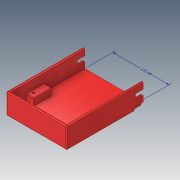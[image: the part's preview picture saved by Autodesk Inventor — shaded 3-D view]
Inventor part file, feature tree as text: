
AUTODESK INVENTOR PART (.ipt)
format: ipt  version: 2019 (Build 230136000, 136)  size: 272,384 bytes
history: native  units: mm
features: extrude x9, sketch x8, plane x3, projected_geometry x3, other x2, fillet x2
ambient origin geometry x8: Origin, YZ Plane, XZ Plane, XY Plane, X Axis, Y Axis, Z Axis, Center Point
bodies: Solid1 (feature_tree)
feature tree (27):
  other  "Annotations"
  extrude  "Extrusion1"  Depth=150.0mm
  extrude  "Extrusion2"  Depth=5.0mm
  extrude  "Extrusion3"  Depth=38.7mm TaperAngle=0.0deg
  sketch  "Sketch6"  dims[d9=3.0mm d10=20.0mm d11=0.0mm]
  fillet  "Fillet1"  Radius=3.0mm
  plane  "Work Plane4"
  extrude  "Extrusion8"  Depth=20.0mm TaperAngle=0.0deg
  extrude  "Extrusion9"  Depth=2.5mm TaperAngle=0.0deg
  fillet  "Fillet4"  Radius=35.0mm
  extrude  "Extrusion10"  Depth=16.0mm
  plane  "Work Plane5"
  extrude  "Extrusion11"  TaperAngle=0.0deg  [1 undecoded]
  plane  "Work Plane3"
  extrude  "Extrusion13"  Depth=40.0mm
  extrude  "Extrusion14"  Depth=16.0mm
  sketch  "Sketch1"  dims[d0=135.0mm d1=150.0mm]
  sketch  "Sketch3"  dims[d2=8.0mm d3=0.0mm d4=5.0mm]
  projected_geometry  "Projected Loop2"
  sketch  "Sketch4"  dims[d5=5.0mm d6=38.7mm d7=0.0mm d8=3.0mm]
  projected_geometry  "Projected Loop3"
  sketch  "Sketch15"  dims[d25=2.0mm d37=2.5mm d38=0.0mm d39=35.0mm]
  projected_geometry  "Projected Loop7"
  sketch  "Sketch16"  dims[d40=0.0mm d41=16.0mm]
  sketch  "Sketch17"  dims[d42=40.0mm d43=0.0mm]
  sketch  "Sketch21"  dims[d44=0.0mm d45=40.0mm d46=16.0mm d47=16.0mm d48=0.0mm d49=1.0mm d50=4.5mm d51=6.0mm d52=9.0mm d53=4.5mm d54=7.0mm d56=12.0mm d57=0.0mm d60=4.5mm d61=4.5mm d62=30.8mm d65=0.0mm d66=0.0mm d67=100.0mm d76=-1.5mm d78=7.5mm d79=7.5mm d80=3.15mm d81=0.0mm d90=12.5mm d91=18.0mm d92=13.0mm d93=17.0mm d94=12.0mm d95=10.0mm d96=0.0mm d73=4.870635mm d74=1.41766mm d75=125.0mm]
  other  "Linear Dimension 1"
note: 1 required parameter value undecoded (feature->parameter linkage not recoverable at this tier; creation-order binding heuristic only, values carry confidence <= 0.55)
